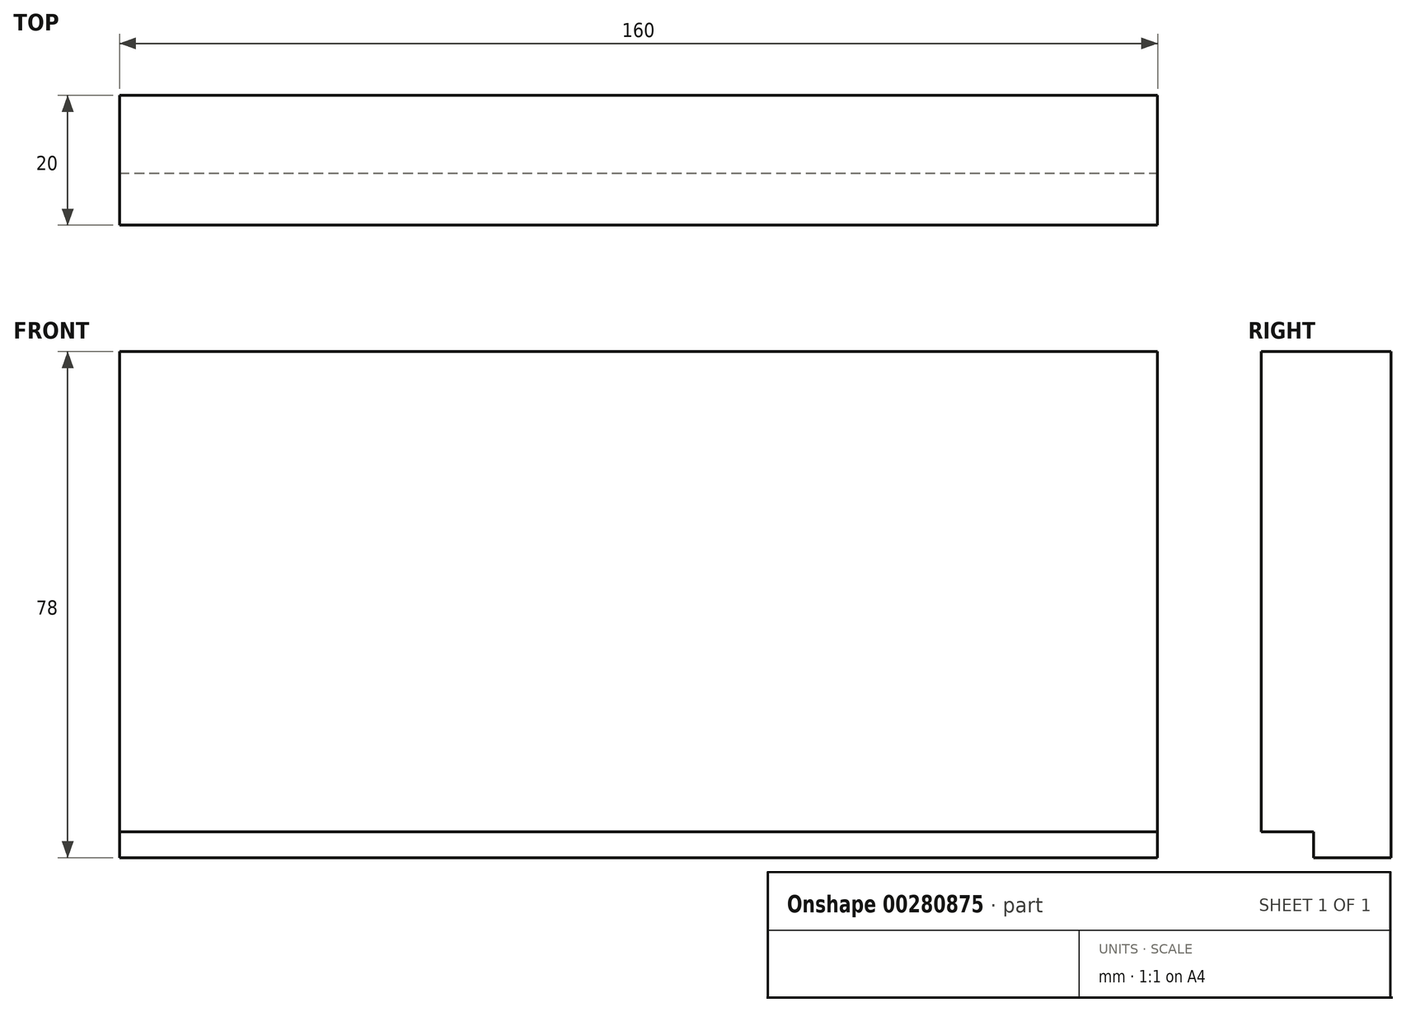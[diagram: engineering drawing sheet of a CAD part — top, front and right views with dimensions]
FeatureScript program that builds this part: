
annotation { "Feature Type Name" : "Feature", "Feature Type Description" : "" }
export const myFeature = defineFeature(function(context is Context, id is Id, definition is map)
    precondition{}
    {
        {
            var Q0;
            Q0=qCreatedBy(makeId("Front.planeOp"),FACE);
            var sketch = newSketch(context, id + "F0", { "sketchPlane" : qUnion([Q0])});
            skLineSegment(sketch, "E0.bottom", {"start": v(-61.27, -41.78) * mm, "end": v(98.73, -41.78) * mm});
            skLineSegment(sketch, "E0.top", {"start": v(-61.27, 36.22) * mm, "end": v(98.73, 36.22) * mm});
            skLineSegment(sketch, "E0.left", {"start": v(-61.27, -41.78) * mm, "end": v(-61.27, 36.22) * mm});
            skLineSegment(sketch, "E0.right", {"start": v(98.73, -41.78) * mm, "end": v(98.73, 36.22) * mm});
            skSolve(sketch);
        }
        {
            var Q0;
            Q0=makeQuery(id+"F0.imprint","IMPRINT",FACE,{"disambiguationData":[TD([[makeQuery(id+"F0.imprint","IMPRINT",EDGE,{"derivedFrom":sQuery(id+"F0.wireOp",EDGE,"E0.bottom")}),1.0]])]});
            extrude(context, id + "F1", {"entities" : qUnion([Q0]), "depth" : 20 * mm});
        }
        {
            var Q0;
            Q0=makeQuery(id+"F1.opExtrude","SWEPT_FACE",FACE,{"disambiguationData":[OSD([sQuery(id+"F0.wireOp",EDGE,"E0.right")])]});
            var sketch = newSketch(context, id + "F2", { "sketchPlane" : qUnion([Q0])});
            skLineSegment(sketch, "E1.bottom", {"start": v(-20, -41.78) * mm, "end": v(-12, -41.78) * mm});
            skLineSegment(sketch, "E1.top", {"start": v(-20, -37.78) * mm, "end": v(-12, -37.78) * mm});
            skLineSegment(sketch, "E1.left", {"start": v(-20, -41.78) * mm, "end": v(-20, -37.78) * mm});
            skLineSegment(sketch, "E1.right", {"start": v(-12, -41.78) * mm, "end": v(-12, -37.78) * mm});
            skSolve(sketch);
        }
        {
            var Q0;
            Q0=makeQuery(id+"F2.imprint","IMPRINT",FACE,{"disambiguationData":[TD([[makeQuery(id+"F2.imprint","IMPRINT",EDGE,{"derivedFrom":sQuery(id+"F2.wireOp",EDGE,"E1.bottom")}),1.0]])]});
            extrude(context, id + "F3", {"entities" : qUnion([Q0]), "operationType" : NewBodyOperationType.REMOVE, "endBound" : BoundingType.UP_TO_NEXT, "oppositeDirection" : true, "depth" : 25 * mm});
        }
    });
